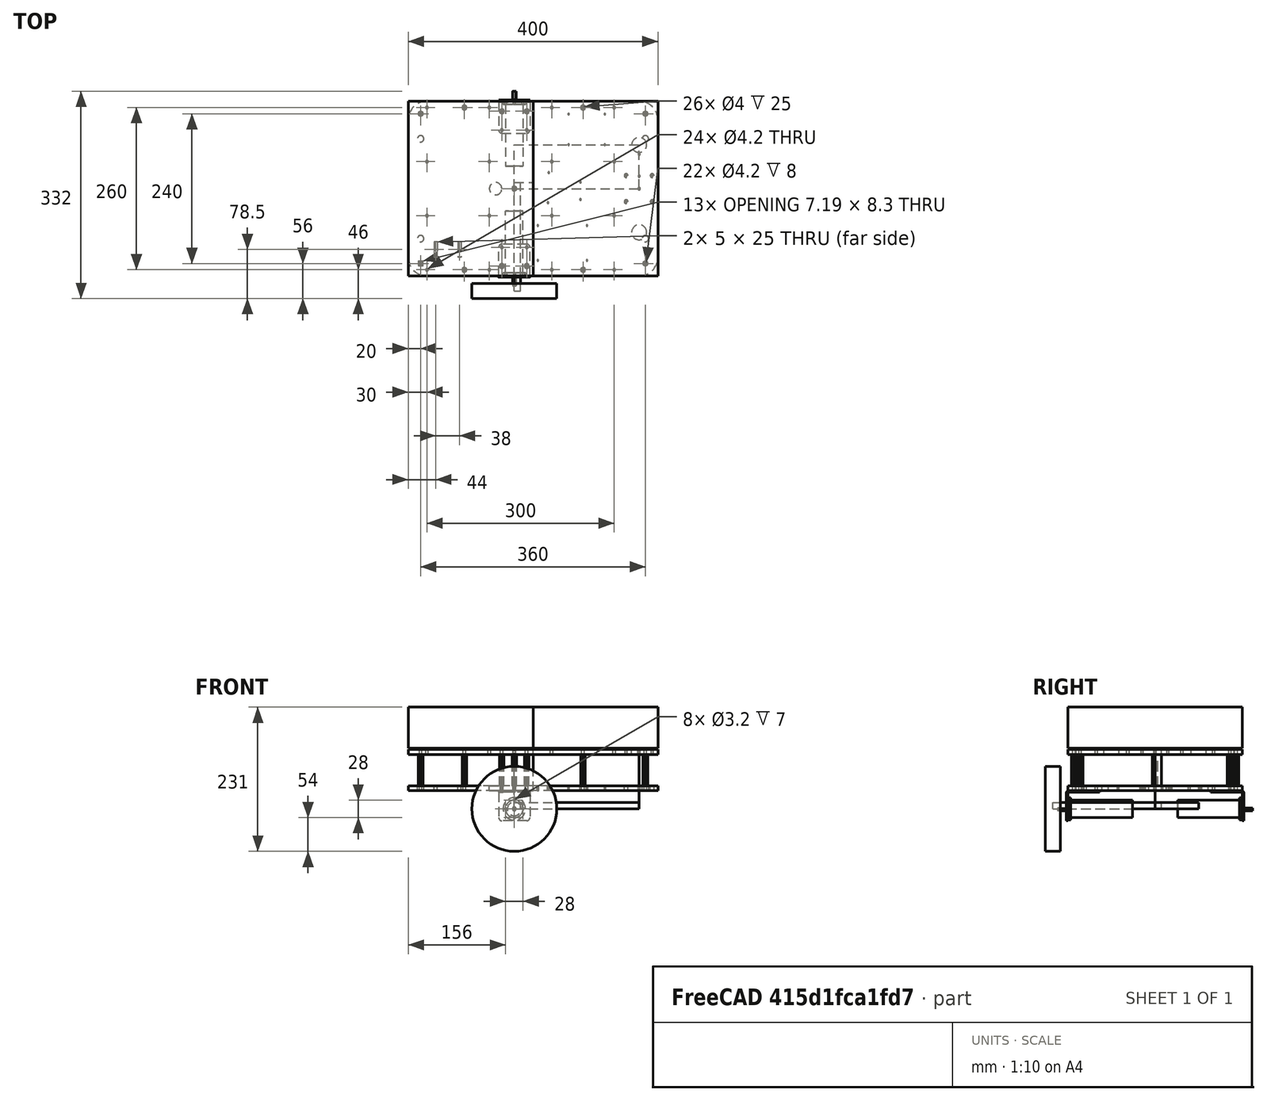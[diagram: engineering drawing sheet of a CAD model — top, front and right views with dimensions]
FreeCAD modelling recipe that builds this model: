
FCSTD DOCUMENT  (FreeCAD 0.16R6703 (Git))
Label: mnwlk3r_urdf
License: All rights reserved
LicenseURL: http://en.wikipedia.org/wiki/All_rights_reserved
objects: Part::Box×8, Part::Feature×1, Part::Cylinder×1
note: 10 computed .brp shape members not serialized (recipe doc carries the construction recipe); baked Part::Feature solids carry a one-line shape summary decoded from their .brp

FEATURE [Part::Feature] Fusion013  label="mnwlk3r_base_"
  Placement = pos=(0,-140,0) rot=(0,0,1;1.5708rad)
  shape: bbox 400 x 312 x 114 mm, 408 faces, 2 solids (baked)
  expr: Placement.Base.y = -280 / 2
FEATURE [Part::Box] Box  label="mnwlk3r_envolppe_"
  Height = 66
  Length = 400
  Placement = pos=(-170,-140,97) rot=(0,0,1;0rad)
  Width = 280
  expr: Placement.Base.z = 29 + 136 / 2
  expr: Placement.Base.y = -280 / 2
FEATURE [Part::Box] Box001  label="mnwlk3r_envolppe_001"
  Height = 66
  Length = 200
  Placement = pos=(-170,-140,97) rot=(0,0,1;0rad)
  Width = 280
FEATURE [Part::Box] Box002  label="mnwlk3r_envolppe_002"
  Height = 66
  Length = 30
  Placement = pos=(0,0,29) rot=(0,0,1;0rad)
  Width = 10
FEATURE [Part::Box] Box003  label="mnwlk3r_envolppe_003"
  Height = 66
  Length = 30
  Placement = pos=(0,0,29) rot=(0,0,1;0rad)
  Width = 10
FEATURE [Part::Box] Box004  label="center_of_the_model_"
  Height = 10
  Length = 10
  Width = 10
FEATURE [Part::Cylinder] Cylinder  label="wheel_136x24_"
  Angle = 360
  Height = 24
  Placement = pos=(0,-152,0) rot=(1,0,0;1.5708rad)
  Radius = 68
  expr: Placement.Base.y = -280 / 2 - 12
FEATURE [Part::Box] Box005  label="caster_wheel_xy_"
  Height = 10
  Length = 200
  Width = 70
FEATURE [Part::Box] Box006  label="lidar_xyz_"
  Height = 95
  Length = 200
  Width = 0.01
FEATURE [Part::Box] Box007  label="distance_between_wheel_half_"
  Height = 10
  Length = 10
  Placement = pos=(0,-164,0) rot=(0,0,1;0rad)
  Width = 164
